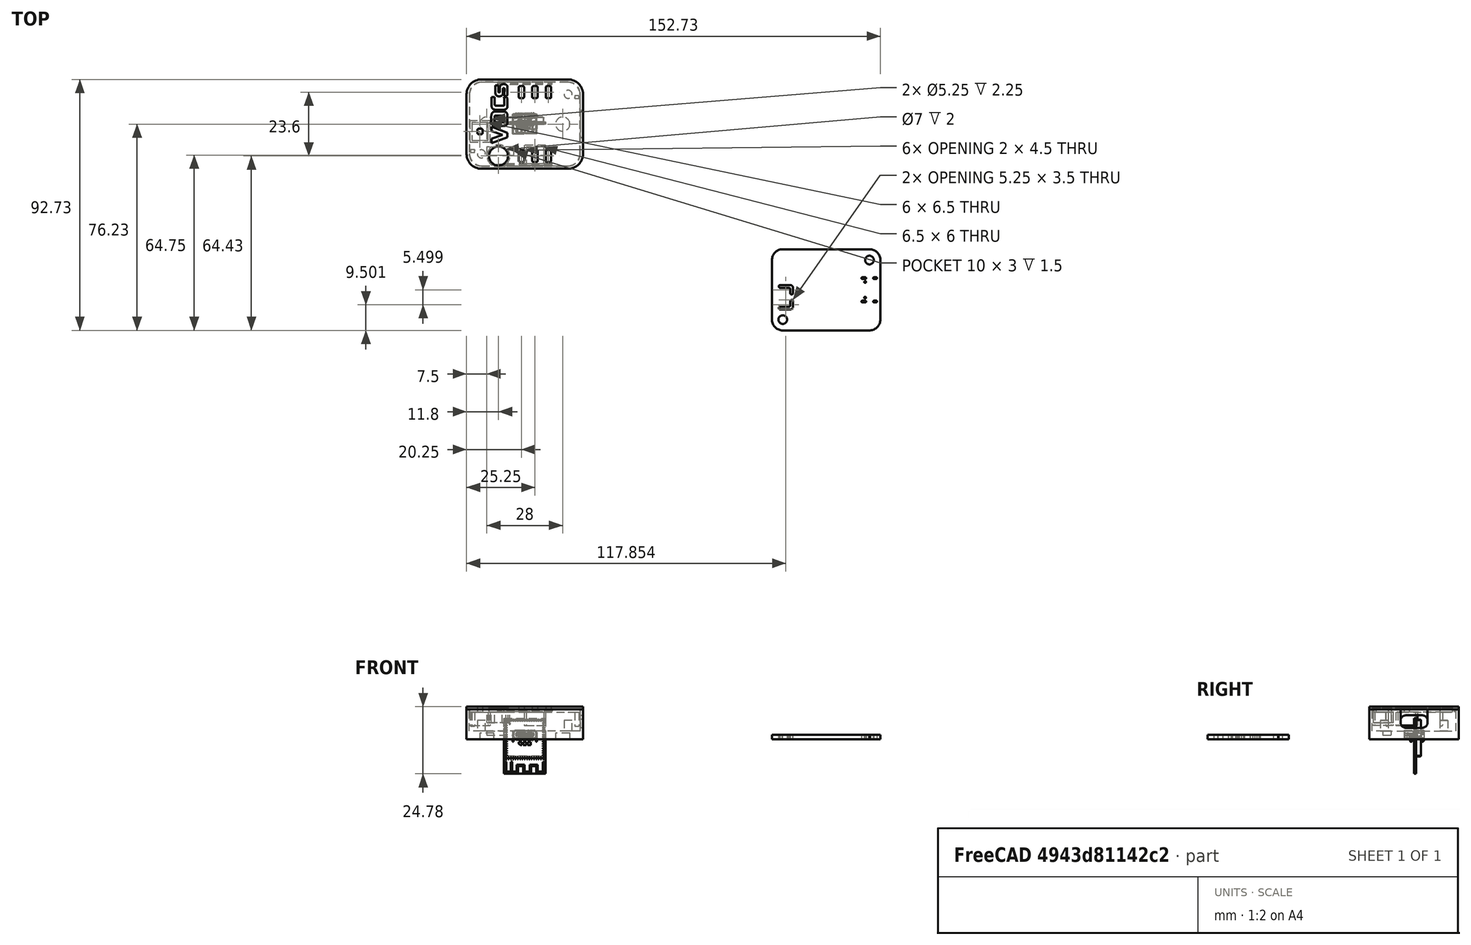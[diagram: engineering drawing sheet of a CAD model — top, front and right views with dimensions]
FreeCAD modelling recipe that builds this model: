
FCSTD DOCUMENT  (FreeCAD 1.0R39109 (Git))
Label: VOCaware_housing
License: All rights reserved
LicenseURL: http://en.wikipedia.org/wiki/All_rights_reserved
objects: Part::Part2DObjectPython×46, Part::Extrusion×36, Part::Feature×28, App::Part×28, Part::Cut×21, Part::Fillet×5, Part::Chamfer×2, Spreadsheet::Sheet×1, App::LinkGroup×1, Part::Fuse×1
note: 139 computed .brp shape members not serialized (recipe doc carries the construction recipe); baked Part::Feature solids carry a one-line shape summary decoded from their .brp

FEATURE [Part::Feature] Part__Feature  label="C_0402_1005Metric"
  shape: bbox 1 x 0.5 x 0.5 mm, 28 faces (baked)
FEATURE [App::Part] C_0402_1005Metric  label="C_0402_1005Metric001"
  Group = -> [Part__Feature]
  Origin = -> Origin
  Placement = pos=(121.23,-72.75,1.65) rot=(0,0,-1;1.5708rad)
FEATURE [Part::Feature] Part__Feature001  label="C_0402_1005Metric002"
  shape: bbox 1 x 0.5 x 0.5 mm, 28 faces (baked)
FEATURE [App::Part] C_0402_1005Metric001  label="C_0402_1005Metric003"
  Group = -> [Part__Feature001]
  Origin = -> Origin001
  Placement = pos=(94.73,-61.98,1.65) rot=(0,0,1;3.14159rad)
FEATURE [Part::Feature] Part__Feature002  label="R_0402_1005Metric"
  shape: bbox 1 x 0.5 x 0.35 mm, 26 faces (baked)
FEATURE [App::Part] R_0402_1005Metric  label="R_0402_1005Metric001"
  Group = -> [Part__Feature002]
  Origin = -> Origin002
  Placement = pos=(126.23,-67.72,1.65) rot=(0,0,1;1.5708rad)
FEATURE [Part::Feature] Part__Feature003  label="R_0402_1005Metric002"
  shape: bbox 1 x 0.5 x 0.35 mm, 26 faces (baked)
FEATURE [App::Part] R_0402_1005Metric001  label="R_0402_1005Metric003"
  Group = -> [Part__Feature003]
  Origin = -> Origin003
  Placement = pos=(119.23,-55.23,1.65) rot=(0,0,1;1.5708rad)
FEATURE [Part::Feature] Part__Feature004  label="C_0402_1005Metric004"
  shape: bbox 1 x 0.5 x 0.5 mm, 28 faces (baked)
FEATURE [App::Part] C_0402_1005Metric002  label="C_0402_1005Metric005"
  Group = -> [Part__Feature004]
  Origin = -> Origin004
  Placement = pos=(121.23,-63.23,1.65) rot=(0,0,1;0rad)
FEATURE [Part::Feature] Part__Feature005  label="R_0402_1005Metric004"
  shape: bbox 1 x 0.5 x 0.35 mm, 26 faces (baked)
FEATURE [App::Part] R_0402_1005Metric002  label="R_0402_1005Metric005"
  Group = -> [Part__Feature005]
  Origin = -> Origin005
  Placement = pos=(100.48,-65.73,1.65) rot=(0,0,1;1.5708rad)
FEATURE [Part::Feature] Part__Feature006  label="R_0402_1005Metric006"
  shape: bbox 1 x 0.5 x 0.35 mm, 26 faces (baked)
FEATURE [App::Part] R_0402_1005Metric003  label="R_0402_1005Metric007"
  Group = -> [Part__Feature006]
  Origin = -> Origin006
  Placement = pos=(114.23,-70.78,1.65) rot=(0,0,1;3.14159rad)
FEATURE [Part::Feature] Part__Feature007  label="C_0402_1005Metric006"
  shape: bbox 1 x 0.5 x 0.5 mm, 28 faces (baked)
FEATURE [App::Part] C_0402_1005Metric003  label="C_0402_1005Metric007"
  Group = -> [Part__Feature007]
  Origin = -> Origin007
  Placement = pos=(117.48,-73.78,1.65) rot=(0,0,-1;1.5708rad)
FEATURE [Part::Feature] Part__Feature008  label="R_0402_1005Metric008"
  shape: bbox 1 x 0.5 x 0.35 mm, 26 faces (baked)
FEATURE [App::Part] R_0402_1005Metric004  label="R_0402_1005Metric009"
  Group = -> [Part__Feature008]
  Origin = -> Origin008
  Placement = pos=(104.48,-70.98,1.65) rot=(0,0,1;1.5708rad)
FEATURE [Part::Feature] Part__Feature009  label="SOT_23"
  shape: bbox 2.5 x 3 x 1.2 mm, 76 faces (baked)
FEATURE [App::Part] SOT_23  label="SOT-23"
  Group = -> [Part__Feature009]
  Origin = -> Origin009
  Placement = pos=(107.293,-72.93,1.65) rot=(0,0,1;3.14159rad)
FEATURE [Part::Feature] Part__Feature010  label="ASSEMBLY"
  shape: bbox 2.54 x 2.44 x 0.95 mm, 50 faces, 8 solids (baked)
FEATURE [App::Part] SGP40_D_R4  label="SGP40-D-R4"
  Group = -> [Part__Feature010]
  Origin = -> Origin010
  Placement = pos=(114.98,-73.03,1.65) rot=(0,0,1;0rad)
FEATURE [Part::Feature] Part__Feature011  label="R_0402_1005Metric010"
  shape: bbox 1 x 0.5 x 0.35 mm, 26 faces (baked)
FEATURE [App::Part] R_0402_1005Metric005  label="R_0402_1005Metric011"
  Group = -> [Part__Feature011]
  Origin = -> Origin011
  Placement = pos=(127.23,-67.72,1.65) rot=(0,0,1;1.5708rad)
FEATURE [Part::Feature] Part__Feature012  label="C_0402_1005Metric008"
  shape: bbox 1 x 0.5 x 0.5 mm, 28 faces (baked)
FEATURE [App::Part] C_0402_1005Metric004  label="C_0402_1005Metric009"
  Group = -> [Part__Feature012]
  Origin = -> Origin012
  Placement = pos=(119.73,-63.5,1.65) rot=(0,0,-1;1.5708rad)
FEATURE [Part::Feature] Part__Feature013  label="C_0603_1608Metric"
  shape: bbox 1.6 x 0.8 x 0.8 mm, 28 faces (baked)
FEATURE [App::Part] C_0603_1608Metric  label="C_0603_1608Metric001"
  Group = -> [Part__Feature013]
  Origin = -> Origin013
  Placement = pos=(100.23,-55.23,1.65) rot=(0,0,1;1.5708rad)
FEATURE [Part::Feature] Part__Feature014  label="R_0402_1005Metric012"
  shape: bbox 1 x 0.5 x 0.35 mm, 26 faces (baked)
FEATURE [App::Part] R_0402_1005Metric006  label="R_0402_1005Metric013"
  Group = -> [Part__Feature014]
  Origin = -> Origin014
  Placement = pos=(100.48,-63.23,1.65) rot=(0,0,-1;1.5708rad)
FEATURE [Part::Feature] Part__Feature015  label="R_0402_1005Metric014"
  shape: bbox 1 x 0.5 x 0.35 mm, 26 faces (baked)
FEATURE [App::Part] R_0402_1005Metric007  label="R_0402_1005Metric015"
  Group = -> [Part__Feature015]
  Origin = -> Origin015
  Placement = pos=(104.48,-73.23,1.65) rot=(0,0,-1;1.5708rad)
FEATURE [Part::Feature] Part__Feature016  label="C_0402_1005Metric010"
  shape: bbox 1 x 0.5 x 0.5 mm, 28 faces (baked)
FEATURE [App::Part] C_0402_1005Metric005  label="C_0402_1005Metric011"
  Group = -> [Part__Feature016]
  Origin = -> Origin016
  Placement = pos=(112.48,-72.78,1.65) rot=(0,0,-1;1.5708rad)
FEATURE [Part::Feature] Part__Feature017  label="USB_C_Receptacle_16P_TopMnt_Horizontal_GCT_USB4105-xx-A"
  shape: bbox 8.94 x 7.78 x 4.26 mm, 646 faces, 36 solids (baked)
FEATURE [App::Part] USB_C_Receptacle_GCT_USB4105_xx_A_16P_TopMnt_Horizontal  label="USB_C_Receptacle_GCT_USB4105-xx-A_16P_TopMnt_Horizontal"
  Group = -> [Part__Feature017]
  Origin = -> Origin017
  Placement = pos=(128.23,-61.23,1.65) rot=(0,0,1;1.5708rad)
FEATURE [Part::Feature] Part__Feature018  label="ASSEMBLY001"
  shape: bbox 4.91 x 3.65 x 1.6 mm, 42 faces, 7 solids (baked)
FEATURE [App::Part] PTS820J25MSMTRLFS
  Group = -> [Part__Feature018]
  Origin = -> Origin018
  Placement = pos=(126.23,-72.23,1.65) rot=(0,0,1;3.14159rad)
FEATURE [Part::Feature] Part__Feature019  label="C_0402_1005Metric012"
  shape: bbox 1 x 0.5 x 0.5 mm, 28 faces (baked)
FEATURE [App::Part] C_0402_1005Metric006  label="C_0402_1005Metric013"
  Group = -> [Part__Feature019]
  Origin = -> Origin019
  Placement = pos=(100.23,-58.23,1.65) rot=(0,0,-1;1.5708rad)
FEATURE [Part::Feature] Part__Feature020  label="R_0402_1005Metric016"
  shape: bbox 1 x 0.5 x 0.35 mm, 26 faces (baked)
FEATURE [App::Part] R_0402_1005Metric008  label="R_0402_1005Metric017"
  Group = -> [Part__Feature020]
  Origin = -> Origin020
  Placement = pos=(109.98,-72.73,1.65) rot=(0,0,1;1.5708rad)
FEATURE [Part::Feature] Part__Feature021  label="C_0402_1005Metric014"
  shape: bbox 1 x 0.5 x 0.5 mm, 28 faces (baked)
FEATURE [App::Part] C_0402_1005Metric007  label="C_0402_1005Metric015"
  Group = -> [Part__Feature021]
  Origin = -> Origin021
  Placement = pos=(119.23,-53.23,1.65) rot=(0,0,1;1.5708rad)
FEATURE [Part::Feature] Part__Feature022  label="C_0402_1005Metric016"
  shape: bbox 1 x 0.5 x 0.5 mm, 28 faces (baked)
FEATURE [App::Part] C_0402_1005Metric008  label="C_0402_1005Metric017"
  Group = -> [Part__Feature022]
  Origin = -> Origin022
  Placement = pos=(121.23,-53.75,1.65) rot=(0,0,1;1.5708rad)
FEATURE [Part::Feature] Part__Feature023  label="ESP32-S3-MINI-1-N8"
  shape: bbox 15.4 x 2.552 x 20.5 mm, 1094 faces, 98 solids (baked)
FEATURE [App::Part] ESP32_S3_MINI_1_N8  label="ESP32-S3-MINI-1-N009"
  Group = -> [Part__Feature023]
  Origin = -> Origin023
  Placement = pos=(109.93,-60.2,1.65) rot=(1,0,0;1.5708rad)
FEATURE [Part::Feature] Part__Feature024  label="C_0402_1005Metric018"
  shape: bbox 1 x 0.5 x 0.5 mm, 28 faces (baked)
FEATURE [App::Part] C_0402_1005Metric009  label="C_0402_1005Metric019"
  Group = -> [Part__Feature024]
  Origin = -> Origin024
  Placement = pos=(101.96,-70.48,1.65) rot=(0,0,1;3.14159rad)
FEATURE [Part::Feature] Part__Feature025  label="Fuse_0603_1608Metric"
  shape: bbox 1.6 x 0.8 x 0.45 mm, 26 faces (baked)
FEATURE [App::Part] Fuse_0603_1608Metric  label="Fuse_0603_1608Metric001"
  Group = -> [Part__Feature025]
  Origin = -> Origin025
  Placement = pos=(121.692,-57.48,1.65) rot=(0,0,1;0rad)
FEATURE [Part::Feature] Part__Feature026  label="ASSEMBLY002"
  shape: bbox 1.84 x 1.5 x 0.69 mm, 30 faces, 5 solids (baked)
FEATURE [App::Part] SHT40_AD1F_R2  label="SHT40-AD1F-R2"
  Group = -> [Part__Feature026]
  Origin = -> Origin026
  Placement = pos=(94.78,-64.03,1.65) rot=(0,0,1;1.5708rad)
FEATURE [Part::Feature] Part__Feature027  label="VOCaware_PCB"
  shape: bbox 40 x 30 x 1.6 mm, 58 faces (baked)
FEATURE [App::Part] VOCaware_1  label="VOCaware 1"
  Group = -> [C_0402_1005Metric,C_0402_1005Metric001,R_0402_1005Metric,R_0402_1005Metric001,C_0402_1005Metric002,R_0402_1005Metric002,R_0402_1005Metric003,C_0402_1005Metric003,R_0402_1005Metric004,SOT_23,SGP40_D_R4,R_0402_1005Metric005,C_0402_1005Metric004,C_0603_1608Metric,R_0402_1005Metric006,R_0402_1005Metric007,C_0402_1005Metric005,USB_C_Receptacle_GCT_USB4105_xx_A_16P_TopMnt_Horizontal,PTS820J25MSMTRLFS,+9 more]
  Origin = -> Origin027
  Placement = pos=(-111.22,61.23,3) rot=(0,0,1;0rad)
  expr: .Placement.Base.x = -111.22 mm
  expr: .Placement.Base.y = 61.23 mm
  expr: .Placement.Base.z = <<params>>.housing_back_thickness
FEATURE [Part::Part2DObjectPython] Rectangle  label="pcb_outline"  # Draft 2D object (typed FeaturePython)
  Area = 1186.27
  ChamferSize = 0
  Columns = 1
  FilletRadius = 4
  Height = 30
  Length = 40
  MakeFace = true
  Placement = pos=(-20,-15,0) rot=(0,0,1;0rad)
  Rows = 1
  expr: .Placement.Base.x = -<<params>>.PCB_width / 2
  expr: .Placement.Base.y = -<<params>>.PCB_length / 2
  expr: FilletRadius = <<params>>.PCB_corner_rad
  expr: Height = <<params>>.PCB_length
  expr: Length = <<params>>.PCB_width
FEATURE [Spreadsheet::Sheet] Spreadsheet  label="params"
  cells = A2='PCB_width; B2(PCB_width)==40 mm; D2='mag_diam; E2(mag_diam)==5 mm; G2='clearance; H2(clearance)==0.5 mm; J2='usb_slit_length; K2(usb_slit_length)==10 mm; M2='usb_bot_clearance; N2(usb_bot_clearance)==0.4 mm; A3='PCB_length; B3(PCB_length)==30 mm; D3='mag_height; E3(mag_height)==2 mm; G3='housing_thickness; H3(housing_thickness)==1 mm; J3='usb_slit_height; K3(usb_slit_height)==3.8 mm; M3='sep_thickness; N3(sep_thickness)==0.7 mm; A4='PCB_corner_rad; B4(PCB_corner_rad)==4 mm; D4='magnet_pos_x; E4(mag_pos_x)==14 mm; G4='housing_back_thickness; H4(housing_back_thickness)==3 mm; J4='M3_clearance; K4(M3_clearance)==0.1 mm; A5='PCB_M3; B5(PCB_M3)==3.2 mm; D5='magnet_clearance; E5(mag_clearance)==0.25 mm; G5='housing_middle_height; H5(housing_middle_height)==8 mm; J5='M3_bottom_height; K5(m3_bottom_height)==4 mm; A6='PCB_height; B6(PCB_height)==1.6 mm; A8='sgp_pos_x; B8(sgp_pos_x)==-PCB_width / 2 + 20.5 mm; D8='sht_pos_x; E8(sht_pos_x)==-PCB_width / 2 + 0.48 mm; G8='led_pos_x; H8(led_pos_x)==-PCB_width / 2 + 10.3 mm - led_width / 2; J8='press_fit_pos_x; K8(press_fit_pos_x)==PCB_width / 2 - press_fit_width; A9='sgp_pos_y; B9(sgp_pos_y)==-PCB_length / 2 + 0.52 mm; D9='sht_pos_y; E9(sht_pos_y)==-PCB_length / 2 + 9.02 mm; G9='led_pos_y; H9(led_pos_y)==-PCB_length / 2 + 3.2 mm - led_height / 2; J9='press_fit_pos_y; K9(press_fit_pos_y)==PCB_length / 2 - PCB_corner_rad - clearance - press_fit_height; A10='sgp_width; B10(sgp_width)==6.5 mm; D10='sht_width; E10(sht_width)==6 mm; G10='led_width; H10(led_width)==6.5 mm; J10='press_fit_width; K10(press_fit_width)==1.5 mm; A11='sgp_length; B11(sgp_length)==6 mm; D11='sht_length; E11(sht_length)==6.5 mm; G11='led_height; H11(led_height)==6.5 mm; J11='press_fit_height; K11(press_fit_height)==1 mm; J12='press_fit_length; K12(press_fit_length)==housing_middle_height - lid_inlet_depth - PCB_height - mag_clearance; A13='snap_fit_width; B13(snap_fit_width)==20 mm; D13='lid_clearance; E13(lid_clearance)==0.2 mm; G13='led_circle_dia; H13(led_circle_dia)==7 mm; A14='snap_fit_height; B14(snap_fit_height)==0.6 mm; D14='lid_top_height; E14(lid_top_height)==1 mm; G14='led_cover_thickness; H14(led_cover_thickness)==0.4 mm; A15='snap_fit_depth; B15(snap_fit_depth)==0.6 mm; D15='lid_inlet_depth; E15(lid_inlet_depth)==1 mm; A16='snap_fit_clearance; B16(snap_fit_clearance)==0.1 mm; D16='lid_breakout_offset; E16(lid_breakout_offset)==0 mm; F16=13; A18='gnd_bug_x; B18(gnd_bug_x)==-14 mm; D18='sgp_cutout_width; E18(sgp_cutout_width)==2 mm; G18='sht_cutout_width; H18(sht_cutout_width)==2 mm; A19='gnd_bug_y; B19(gnd_bug_y)==-11.5 mm; D19='sgp_cutout_height; E19(sgp_cutout_height)==4.5 mm; G19='sht_cutout_height; H19(sht_cutout_height)==2 mm; A20='gnd_bug_width; B20(gnd_bug_width)==10 mm; D20='cutout_distance; E20(cutout_distance)==5 mm; G20='led_sep_depth; H20(led_sep_depth)==4 mm; A21='gnd_bug_height; B21(gnd_bug_height)==3 mm; A22='gnd_bug_depth; B22(gnd_bug_depth)==1.5 mm
FEATURE [Part::Part2DObjectPython] Arc  label="pcb_outl_corner_tl"  # Draft 2D object (typed FeaturePython)
  Area = 0
  FirstAngle = 90
  LastAngle = 180
  MakeFace = true
  Placement = pos=(-16,11,0) rot=(0,0,1;0rad)
  Radius = 4
  expr: .Placement.Base.x = -<<params>>.PCB_width / 2 + <<params>>.PCB_corner_rad
  expr: .Placement.Base.y = <<params>>.PCB_length / 2 - <<params>>.PCB_corner_rad
  expr: Radius = <<params>>.PCB_corner_rad
FEATURE [Part::Part2DObjectPython] Arc001  label="pcb_outl_corner_tr"  # Draft 2D object (typed FeaturePython)
  Area = 0
  FirstAngle = 0
  LastAngle = 90
  MakeFace = true
  Placement = pos=(16,11,0) rot=(0,0,1;0rad)
  Radius = 4
  expr: .Placement.Base.x = <<params>>.PCB_width / 2 - <<params>>.PCB_corner_rad
  expr: .Placement.Base.y = <<params>>.PCB_length / 2 - <<params>>.PCB_corner_rad
  expr: Radius = <<params>>.PCB_corner_rad
FEATURE [Part::Part2DObjectPython] Arc002  label="pcb_outl_corner_bl"  # Draft 2D object (typed FeaturePython)
  Area = 0
  FirstAngle = 180
  LastAngle = 270
  MakeFace = true
  Placement = pos=(-16,-11,0) rot=(0,0,1;0rad)
  Radius = 4
  expr: .Placement.Base.x = -<<params>>.PCB_width / 2 + <<params>>.PCB_corner_rad
  expr: .Placement.Base.y = -<<params>>.PCB_length / 2 + <<params>>.PCB_corner_rad
  expr: Radius = <<params>>.PCB_corner_rad
FEATURE [Part::Part2DObjectPython] Arc003  label="pcb_outl_corner_br"  # Draft 2D object (typed FeaturePython)
  Area = 0
  FirstAngle = 270
  LastAngle = 0
  MakeFace = true
  Placement = pos=(16,-11,0) rot=(0,0,1;0rad)
  Radius = 4
  expr: .Placement.Base.x = <<params>>.PCB_width / 2 - <<params>>.PCB_corner_rad
  expr: .Placement.Base.y = -<<params>>.PCB_length / 2 + <<params>>.PCB_corner_rad
  expr: Radius = <<params>>.PCB_corner_rad
FEATURE [Part::Part2DObjectPython] Line  label="pcb_outl_line_l"  # Draft 2D object (typed FeaturePython)
  Area = 0
  ChamferSize = 0
  Closed = false
  End = (-20,11,0)
  FilletRadius = 0
  Length = 22
  MakeFace = true
  Placement = pos=(-20,-11,0) rot=(0,0,1;0rad)
  Points = (2) [(0,0,0),(0,22,0)]
  Start = (-20,-11,0)
  Subdivisions = 0
  expr: .End.x = -<<params>>.PCB_width / 2
  expr: .End.y = <<params>>.PCB_length / 2 - <<params>>.PCB_corner_rad
  expr: .Placement.Base.x = -<<params>>.PCB_width / 2
  expr: .Placement.Base.y = -<<params>>.PCB_length / 2 + <<params>>.PCB_corner_rad
  expr: .Start.x = -<<params>>.PCB_width / 2
  expr: .Start.y = -<<params>>.PCB_length / 2 + <<params>>.PCB_corner_rad
  expr: Length = <<params>>.PCB_length - 2 * <<params>>.PCB_corner_rad
FEATURE [Part::Part2DObjectPython] Line001  label="pcb_outl_line_r"  # Draft 2D object (typed FeaturePython)
  Area = 0
  ChamferSize = 0
  Closed = false
  End = (20,11,0)
  FilletRadius = 0
  Length = 22
  MakeFace = true
  Placement = pos=(-20,-11,0) rot=(0,0,1;0rad)
  Points = (2) [(40,0,0),(40,22,0)]
  Start = (20,-11,0)
  Subdivisions = 0
  expr: .End.x = <<params>>.PCB_width / 2
  expr: .End.y = <<params>>.PCB_length / 2 - <<params>>.PCB_corner_rad
  expr: .Placement.Base.x = -<<params>>.PCB_width / 2
  expr: .Placement.Base.y = -<<params>>.PCB_length / 2 + <<params>>.PCB_corner_rad
  expr: .Start.x = +<<params>>.PCB_width / 2
  expr: .Start.y = -<<params>>.PCB_length / 2 + <<params>>.PCB_corner_rad
  expr: Length = <<params>>.PCB_length - 2 * <<params>>.PCB_corner_rad
FEATURE [Part::Part2DObjectPython] Line002  label="pcb_outl_line_t"  # Draft 2D object (typed FeaturePython)
  Area = 0
  ChamferSize = 0
  Closed = false
  End = (-16,15,0)
  FilletRadius = 0
  Length = 32
  MakeFace = true
  Placement = pos=(-20,-11,0) rot=(0,0,1;0rad)
  Points = (2) [(36,26,0),(4,26,0)]
  Start = (16,15,0)
  Subdivisions = 0
  expr: .End.x = -<<params>>.PCB_width / 2 + <<params>>.PCB_corner_rad
  expr: .End.y = <<params>>.PCB_length / 2
  expr: .Placement.Base.x = -<<params>>.PCB_width / 2
  expr: .Placement.Base.y = -<<params>>.PCB_length / 2 + <<params>>.PCB_corner_rad
  expr: .Start.x = <<params>>.PCB_width / 2 - <<params>>.PCB_corner_rad
  expr: .Start.y = <<params>>.PCB_length / 2
  expr: Length = <<params>>.PCB_width - 2 * <<params>>.PCB_corner_rad
FEATURE [Part::Part2DObjectPython] Line003  label="pcb_outl_line_b"  # Draft 2D object (typed FeaturePython)
  Area = 0
  ChamferSize = 0
  Closed = false
  End = (-16,-15,0)
  FilletRadius = 0
  Length = 32
  MakeFace = true
  Placement = pos=(-20,-11,0) rot=(0,0,1;0rad)
  Points = (2) [(36,-4,0),(4,-4,0)]
  Start = (16,-15,0)
  Subdivisions = 0
  expr: .End.x = -<<params>>.PCB_width / 2 + <<params>>.PCB_corner_rad
  expr: .End.y = -<<params>>.PCB_length / 2
  expr: .Placement.Base.x = -<<params>>.PCB_width / 2
  expr: .Placement.Base.y = -<<params>>.PCB_length / 2 + <<params>>.PCB_corner_rad
  expr: .Start.x = <<params>>.PCB_width / 2 - <<params>>.PCB_corner_rad
  expr: .Start.y = -<<params>>.PCB_length / 2
  expr: Length = <<params>>.PCB_width - 2 * <<params>>.PCB_corner_rad
FEATURE [Part::Part2DObjectPython] Circle  label="m3_bl"  # Draft 2D object (typed FeaturePython)
  Area = 7.06858
  FirstAngle = 0
  LastAngle = 0
  MakeFace = true
  Placement = pos=(-16,-11,3) rot=(0,0,1;0rad)
  Radius = 1.5
  expr: .Placement.Base.x = -<<params>>.PCB_width / 2 + <<params>>.PCB_corner_rad
  expr: .Placement.Base.y = -<<params>>.PCB_length / 2 + <<params>>.PCB_corner_rad
  expr: .Placement.Base.z = <<params>>.housing_back_thickness
  expr: Radius = <<params>>.PCB_M3 / 2 - <<params>>.M3_clearance
FEATURE [Part::Part2DObjectPython] Circle001  label="m3_tr"  # Draft 2D object (typed FeaturePython)
  Area = 7.06858
  FirstAngle = 0
  LastAngle = 0
  MakeFace = true
  Placement = pos=(16,11,3) rot=(0,0,1;0rad)
  Radius = 1.5
  expr: .Placement.Base.x = +<<params>>.PCB_width / 2 - <<params>>.PCB_corner_rad
  expr: .Placement.Base.y = <<params>>.PCB_length / 2 - <<params>>.PCB_corner_rad
  expr: .Placement.Base.z = <<params>>.housing_back_thickness
  expr: Radius = <<params>>.PCB_M3 / 2 - <<params>>.M3_clearance
FEATURE [Part::Part2DObjectPython] Rectangle001  label="inner_housing"  # Draft 2D object (typed FeaturePython)
  Area = 1253.62
  ChamferSize = 0
  Columns = 1
  FilletRadius = 4.5
  Height = 31
  Length = 41
  MakeFace = true
  Placement = pos=(-20.5,-15.5,3) rot=(0,0,1;0rad)
  Rows = 1
  expr: .Placement.Base.x = -<<params>>.PCB_width / 2 - <<params>>.clearance
  expr: .Placement.Base.y = -<<params>>.PCB_length / 2 - <<params>>.clearance
  expr: .Placement.Base.z = <<params>>.housing_back_thickness
  expr: FilletRadius = <<params>>.PCB_corner_rad + <<params>>.clearance
  expr: Height = <<params>>.PCB_length + 2 * <<params>>.clearance
  expr: Length = <<params>>.PCB_width + 2 * <<params>>.clearance
FEATURE [Part::Part2DObjectPython] Rectangle002  label="outer_housing"  # Draft 2D object (typed FeaturePython)
  Area = 1393.03
  ChamferSize = 0
  Columns = 1
  FilletRadius = 5.5
  Height = 33
  Length = 43
  MakeFace = true
  Placement = pos=(-21.5,-16.5,0) rot=(0,0,1;0rad)
  Rows = 1
  expr: .Placement.Base.x = -<<params>>.PCB_width / 2 - <<params>>.clearance - <<params>>.housing_thickness
  expr: .Placement.Base.y = -<<params>>.PCB_length / 2 - <<params>>.clearance - <<params>>.housing_thickness
  expr: FilletRadius = <<params>>.PCB_corner_rad + <<params>>.clearance + <<params>>.housing_thickness
  expr: Height = <<params>>.PCB_length + 2 * <<params>>.clearance + 2 * <<params>>.housing_thickness
  expr: Length = <<params>>.PCB_width + 2 * <<params>>.clearance + 2 * <<params>>.housing_thickness
FEATURE [App::LinkGroup] LinkGroup  label="pcb_outline_detailed"
  ElementList = -> [Arc,Arc001,Arc002,Arc003,Line,Line001,Line002,Line003]
  LinkMode = 0
FEATURE [Part::Part2DObjectPython] Rectangle003  label="usb_slit"  # Draft 2D object (typed FeaturePython)
  Area = 10
  ChamferSize = 0
  Columns = 1
  FilletRadius = 0
  Height = 10
  Length = 1
  MakeFace = true
  Placement = pos=(20.5,-5,4.2) rot=(0,0,1;0rad)
  Rows = 1
  expr: .Placement.Base.x = <<params>>.PCB_width / 2 + <<params>>.clearance
  expr: .Placement.Base.y = -<<params>>.usb_slit_length / 2
  expr: .Placement.Base.z = <<params>>.housing_back_thickness + <<params>>.PCB_height - <<params>>.usb_bot_clearance
  expr: Height = <<params>>.usb_slit_length
  expr: Length = <<params>>.housing_thickness
FEATURE [Part::Part2DObjectPython] Circle002  label="mag_l"  # Draft 2D object (typed FeaturePython)
  Area = 21.6475
  FirstAngle = 0
  LastAngle = 0
  MakeFace = true
  Placement = pos=(14,0,0) rot=(0,0,1;0rad)
  Radius = 2.625
  expr: .Placement.Base.x = <<params>>.mag_pos_x
  expr: Radius = <<params>>.mag_diam / 2 + <<params>>.mag_clearance / 2
FEATURE [Part::Part2DObjectPython] Circle003  label="mag_r"  # Draft 2D object (typed FeaturePython)
  Area = 21.6475
  FirstAngle = 0
  LastAngle = 0
  MakeFace = true
  Placement = pos=(-14,0,0) rot=(0,0,1;0rad)
  Radius = 2.625
  expr: .Placement.Base.x = -<<params>>.mag_pos_x
  expr: Radius = <<params>>.mag_diam / 2 + <<params>>.mag_clearance / 2
FEATURE [Part::Part2DObjectPython] Rectangle004  label="sgp_outline"  # Draft 2D object (typed FeaturePython)
  Area = 39
  ChamferSize = 0
  Columns = 1
  FilletRadius = 0
  Height = 6
  Length = 6.5
  MakeFace = true
  Placement = pos=(0.5,-14.48,10) rot=(0,0,1;0rad)
  Rows = 1
  expr: .Placement.Base.x = <<params>>.sgp_pos_x
  expr: .Placement.Base.y = <<params>>.sgp_pos_y
  expr: .Placement.Base.z = <<params>>.housing_back_thickness + <<params>>.housing_middle_height + <<params>>.lid_breakout_offset - <<params>>.lid_inlet_depth
  expr: Height = <<params>>.sgp_length
  expr: Length = <<params>>.sgp_width
FEATURE [Part::Part2DObjectPython] Rectangle005  label="sht_outline"  # Draft 2D object (typed FeaturePython)
  Area = 39
  ChamferSize = 0
  Columns = 1
  FilletRadius = 0
  Height = 6.5
  Length = 6
  MakeFace = true
  Placement = pos=(-19.52,-5.98,10) rot=(0,0,1;0rad)
  Rows = 1
  expr: .Placement.Base.x = <<params>>.sht_pos_x
  expr: .Placement.Base.y = <<params>>.sht_pos_y
  expr: .Placement.Base.z = <<params>>.housing_back_thickness + <<params>>.housing_middle_height + <<params>>.lid_breakout_offset - <<params>>.lid_inlet_depth
  expr: Height = <<params>>.sht_length
  expr: Length = <<params>>.sht_width
FEATURE [Part::Part2DObjectPython] Rectangle006  label="led_outline"  # Draft 2D object (typed FeaturePython)
  Area = 42.25
  ChamferSize = 0
  Columns = 1
  FilletRadius = 0
  Height = 6.5
  Length = 6.5
  MakeFace = true
  Placement = pos=(-12.95,-15.05,0) rot=(0,0,1;0rad)
  Rows = 1
  expr: .Placement.Base.x = <<params>>.led_pos_x
  expr: .Placement.Base.y = <<params>>.led_pos_y
  expr: Height = <<params>>.led_height
  expr: Length = <<params>>.led_width
FEATURE [Part::Extrusion] Extrude  label="out_extrude"
  Base = -> Rectangle002
  Dir = (0,0,1)
  DirMode = 2
  FaceMakerClass = Part::FaceMakerBullseye
  FaceMakerMode = 3
  LengthFwd = 11
  LengthRev = 0
  Solid = false
  Symmetric = false
  expr: LengthFwd = <<params>>.housing_back_thickness + <<params>>.housing_middle_height
FEATURE [Part::Extrusion] Extrude001  label="in_extrude"
  Base = -> Rectangle001
  Dir = (0,0,1)
  DirMode = 2
  FaceMakerClass = Part::FaceMakerBullseye
  FaceMakerMode = 3
  LengthFwd = 8
  LengthRev = 0
  Solid = false
  Symmetric = false
  expr: LengthFwd = <<params>>.housing_middle_height
FEATURE [Part::Cut] Cut  label="housing_base"
  Base = -> Extrude
  Refine = true
  Tool = -> Extrude001
FEATURE [Part::Extrusion] Extrude002  label="m3_pole_bl"
  Base = -> Circle
  Dir = (0,0,1)
  DirMode = 2
  FaceMakerClass = Part::FaceMakerBullseye
  FaceMakerMode = 3
  LengthFwd = 4
  LengthRev = 0
  Solid = false
  Symmetric = false
  expr: LengthFwd = <<params>>.m3_bottom_height
FEATURE [Part::Extrusion] Extrude003  label="m3_pole_tr"
  Base = -> Circle001
  Dir = (0,0,1)
  DirMode = 2
  FaceMakerClass = Part::FaceMakerBullseye
  FaceMakerMode = 3
  LengthFwd = 4
  LengthRev = 0
  Solid = false
  Symmetric = false
  expr: LengthFwd = <<params>>.m3_bottom_height
FEATURE [Part::Extrusion] Extrude004
  Base = -> Rectangle003
  Dir = (0,0,1)
  DirMode = 2
  FaceMakerClass = Part::FaceMakerBullseye
  FaceMakerMode = 3
  LengthFwd = 6.8
  LengthRev = 0
  Solid = false
  Symmetric = false
  expr: LengthFwd = <<params>>.housing_middle_height - <<params>>.PCB_height + <<params>>.usb_bot_clearance
FEATURE [Part::Fillet] Fillet
  Base = -> Extrude004
  EdgeLinks = -> Extrude004 [Edge3,Edge9]
  Edges = 2 edges r=2: [Edge3,Edge9]
FEATURE [Part::Cut] Cut001  label="usb_slit_cut"
  Base = -> Cut
  Refine = true
  Tool = -> Fillet
FEATURE [Part::Part2DObjectPython] Rectangle007  label="snap_base_top"  # Draft 2D object (typed FeaturePython)
  Area = 12
  ChamferSize = 0
  Columns = 1
  FilletRadius = 0
  Height = 0.6
  Length = 20
  MakeFace = true
  Placement = pos=(-10,14.9,11) rot=(0,0,1;0rad)
  Rows = 1
  expr: .Placement.Base.x = -<<params>>.snap_fit_width / 2
  expr: .Placement.Base.y = <<params>>.PCB_length / 2 + <<params>>.clearance - <<params>>.snap_fit_depth
  expr: .Placement.Base.z = <<params>>.housing_back_thickness + <<params>>.housing_middle_height
  expr: Height = <<params>>.snap_fit_depth
  expr: Length = <<params>>.snap_fit_width
FEATURE [Part::Part2DObjectPython] Rectangle008  label="snap_base_bot"  # Draft 2D object (typed FeaturePython)
  Area = 12
  ChamferSize = 0
  Columns = 1
  FilletRadius = 0
  Height = 0.6
  Length = 20
  MakeFace = true
  Placement = pos=(-10,-15.5,11) rot=(0,0,1;0rad)
  Rows = 1
  expr: .Placement.Base.x = -<<params>>.snap_fit_width / 2
  expr: .Placement.Base.y = -<<params>>.PCB_length / 2 - <<params>>.clearance
  expr: .Placement.Base.z = <<params>>.housing_back_thickness + <<params>>.housing_middle_height
  expr: Height = <<params>>.snap_fit_depth
  expr: Length = <<params>>.snap_fit_width
FEATURE [Part::Extrusion] Extrude005  label="snap_top_extr"
  Base = -> Rectangle007
  Dir = (0,0,1)
  DirMode = 2
  FaceMakerClass = Part::FaceMakerBullseye
  FaceMakerMode = 3
  LengthFwd = -0.6
  LengthRev = 0
  Solid = false
  Symmetric = false
  expr: LengthFwd = -<<params>>.snap_fit_height
FEATURE [Part::Extrusion] Extrude006  label="snap_bot_extr"
  Base = -> Rectangle008
  Dir = (0,0,1)
  DirMode = 2
  FaceMakerClass = Part::FaceMakerBullseye
  FaceMakerMode = 3
  LengthFwd = -0.6
  LengthRev = 0
  Solid = false
  Symmetric = false
  expr: LengthFwd = -<<params>>.snap_fit_height
FEATURE [Part::Chamfer] Chamfer  label="snap_top_Chamfer"
  Base = -> Extrude005
  EdgeLinks = -> Extrude005 [Edge3]
  Edges = 1 edges r=0.5: [Edge3]
FEATURE [Part::Chamfer] Chamfer001  label="snap_bot_Chamfer"
  Base = -> Extrude006
  EdgeLinks = -> Extrude006 [Edge9]
  Edges = 1 edges r=0.5: [Edge9]
FEATURE [Part::Part2DObjectPython] Rectangle009  label="outer_lid"  # Draft 2D object (typed FeaturePython)
  Area = 1393.03
  ChamferSize = 0
  Columns = 1
  FilletRadius = 5.5
  Height = 33
  Length = 43
  MakeFace = true
  Placement = pos=(-21.5,-16.5,11) rot=(0,0,1;0rad)
  Rows = 1
  expr: .Placement.Base.x = -<<params>>.PCB_width / 2 - <<params>>.clearance - <<params>>.housing_thickness
  expr: .Placement.Base.y = -<<params>>.PCB_length / 2 - <<params>>.clearance - <<params>>.housing_thickness
  expr: .Placement.Base.z = <<params>>.housing_back_thickness + <<params>>.housing_middle_height + <<params>>.lid_breakout_offset
  expr: FilletRadius = <<params>>.PCB_corner_rad + <<params>>.clearance + <<params>>.housing_thickness
  expr: Height = <<params>>.PCB_length + 2 * <<params>>.clearance + 2 * <<params>>.housing_thickness
  expr: Length = <<params>>.PCB_width + 2 * <<params>>.clearance + 2 * <<params>>.housing_thickness
FEATURE [Part::Part2DObjectPython] Rectangle010  label="inner_lid"  # Draft 2D object (typed FeaturePython)
  Area = 1239.26
  ChamferSize = 0
  Columns = 1
  FilletRadius = 4.5
  Height = 30.8
  Length = 40.8
  MakeFace = true
  Placement = pos=(-20.4,-15.4,11) rot=(0,0,1;0rad)
  Rows = 1
  expr: .Placement.Base.x = -<<params>>.PCB_width / 2 - <<params>>.clearance + <<params>>.lid_clearance / 2
  expr: .Placement.Base.y = -<<params>>.PCB_length / 2 - <<params>>.clearance + <<params>>.lid_clearance / 2
  expr: .Placement.Base.z = <<params>>.housing_back_thickness + <<params>>.housing_middle_height + <<params>>.lid_breakout_offset
  expr: FilletRadius = <<params>>.PCB_corner_rad + <<params>>.clearance
  expr: Height = <<params>>.PCB_length + 2 * <<params>>.clearance - <<params>>.lid_clearance
  expr: Length = <<params>>.PCB_width + 2 * <<params>>.clearance - <<params>>.lid_clearance
FEATURE [Part::Extrusion] Extrude007  label="lid_top"
  Base = -> Rectangle009
  Dir = (0,0,1)
  DirMode = 2
  FaceMakerClass = Part::FaceMakerBullseye
  FaceMakerMode = 3
  LengthFwd = 1
  LengthRev = 0
  Solid = false
  Symmetric = false
  expr: LengthFwd = <<params>>.lid_top_height
FEATURE [Part::Extrusion] Extrude008  label="lid_bot"
  Base = -> Rectangle010
  Dir = (0,0,1)
  DirMode = 2
  FaceMakerClass = Part::FaceMakerBullseye
  FaceMakerMode = 3
  LengthFwd = -1
  LengthRev = 0
  Solid = false
  Symmetric = false
  expr: LengthFwd = -<<params>>.lid_inlet_depth
FEATURE [Part::Part2DObjectPython] Rectangle011  label="snap_lid_top"  # Draft 2D object (typed FeaturePython)
  Area = 14.14
  ChamferSize = 0
  Columns = 1
  FilletRadius = 0
  Height = 0.7
  Length = 20.2
  MakeFace = true
  Placement = pos=(-10.1,14.7,11) rot=(0,0,1;0rad)
  Rows = 1
  expr: .Placement.Base.x = -<<params>>.snap_fit_width / 2 - <<params>>.snap_fit_clearance
  expr: .Placement.Base.y = <<params>>.PCB_length / 2 + <<params>>.clearance - <<params>>.snap_fit_depth - <<params>>.snap_fit_clearance - <<params>>.lid_clearance / 2
  expr: .Placement.Base.z = <<params>>.housing_back_thickness + <<params>>.housing_middle_height + <<params>>.lid_breakout_offset
  expr: Height = <<params>>.snap_fit_depth + <<params>>.snap_fit_clearance
  expr: Length = <<params>>.snap_fit_width + 2 * <<params>>.snap_fit_clearance
FEATURE [Part::Part2DObjectPython] Rectangle012  label="snap_lid_bot"  # Draft 2D object (typed FeaturePython)
  Area = 14.14
  ChamferSize = 0
  Columns = 1
  FilletRadius = 0
  Height = 0.7
  Length = 20.2
  MakeFace = true
  Placement = pos=(-10.1,-15.4,11) rot=(0,0,1;0rad)
  Rows = 1
  expr: .Placement.Base.x = -<<params>>.snap_fit_width / 2 - <<params>>.snap_fit_clearance
  expr: .Placement.Base.y = -<<params>>.PCB_length / 2 - <<params>>.clearance + <<params>>.lid_clearance / 2
  expr: .Placement.Base.z = <<params>>.housing_back_thickness + <<params>>.housing_middle_height + <<params>>.lid_breakout_offset
  expr: Height = <<params>>.snap_fit_depth + <<params>>.snap_fit_clearance
  expr: Length = <<params>>.snap_fit_width + 2 * <<params>>.snap_fit_clearance
FEATURE [Part::Extrusion] Extrude009
  Base = -> Rectangle011
  Dir = (0,0,1)
  DirMode = 2
  FaceMakerClass = Part::FaceMakerBullseye
  FaceMakerMode = 3
  LengthFwd = -0.7
  LengthRev = 0
  Solid = false
  Symmetric = false
  expr: LengthFwd = -<<params>>.snap_fit_height - <<params>>.snap_fit_clearance
FEATURE [Part::Extrusion] Extrude010
  Base = -> Rectangle012
  Dir = (0,0,1)
  DirMode = 2
  FaceMakerClass = Part::FaceMakerBullseye
  FaceMakerMode = 3
  LengthFwd = -0.7
  LengthRev = 0
  Solid = false
  Symmetric = false
  expr: LengthFwd = -<<params>>.snap_fit_height - <<params>>.snap_fit_clearance
FEATURE [Part::Cut] Cut002
  Base = -> Extrude008
  Refine = true
  Tool = -> Extrude009
FEATURE [Part::Cut] Cut003  label="lid_snap_cut"
  Base = -> Cut002
  Refine = true
  Tool = -> Extrude010
FEATURE [Part::Extrusion] Extrude011  label="mag_l_extr"
  Base = -> Circle002
  Dir = (0,0,1)
  DirMode = 2
  FaceMakerClass = Part::FaceMakerBullseye
  FaceMakerMode = 3
  LengthFwd = 2.25
  LengthRev = 0
  Solid = false
  Symmetric = false
  expr: LengthFwd = <<params>>.mag_height + <<params>>.mag_clearance
FEATURE [Part::Extrusion] Extrude012  label="mag_r_extr"
  Base = -> Circle003
  Dir = (0,0,1)
  DirMode = 2
  FaceMakerClass = Part::FaceMakerBullseye
  FaceMakerMode = 3
  LengthFwd = 2.25
  LengthRev = 0
  Solid = false
  Symmetric = false
  expr: LengthFwd = <<params>>.mag_height + <<params>>.mag_clearance
FEATURE [Part::Cut] Cut004
  Base = -> Cut001
  Refine = true
  Tool = -> Extrude011
FEATURE [Part::Cut] Cut005  label="bot_w_mag_holes"
  Base = -> Cut004
  Refine = true
  Tool = -> Extrude012
FEATURE [Part::Part2DObjectPython] Rectangle013  label="usb_slit001"  # Draft 2D object (typed FeaturePython)
  Area = 10
  ChamferSize = 0
  Columns = 1
  FilletRadius = 0
  Height = 10
  Length = 1
  MakeFace = true
  Placement = pos=(20.5,-5,4.2) rot=(0,0,1;0rad)
  Rows = 1
  expr: .Placement.Base.x = <<params>>.PCB_width / 2 + <<params>>.clearance
  expr: .Placement.Base.y = -<<params>>.usb_slit_length / 2
  expr: .Placement.Base.z = <<params>>.housing_back_thickness + <<params>>.PCB_height - <<params>>.usb_bot_clearance
  expr: Height = <<params>>.usb_slit_length
  expr: Length = <<params>>.housing_thickness
FEATURE [Part::Extrusion] Extrude013
  Base = -> Rectangle013
  Dir = (0,0,1)
  DirMode = 2
  FaceMakerClass = Part::FaceMakerBullseye
  FaceMakerMode = 3
  LengthFwd = 4.6
  LengthRev = 0
  Solid = false
  Symmetric = false
  expr: LengthFwd = <<params>>.usb_slit_height + 2 * <<params>>.usb_bot_clearance
FEATURE [Part::Fillet] Fillet001
  Base = -> Extrude013
  EdgeLinks = -> Extrude013 [Edge3,Edge9]
  Edges = 2 edges r=2: [Edge3,Edge9]
FEATURE [Part::Fillet] Fillet002
  Base = -> Fillet001
  EdgeLinks = -> Fillet001 [Edge3,Edge13]
  Edges = 2 edges r=2: [Edge3,Edge13]
FEATURE [Part::Part2DObjectPython] Rectangle014  label="usb_slit002"  # Draft 2D object (typed FeaturePython)
  Area = 9.8
  ChamferSize = 0
  Columns = 1
  FilletRadius = 0
  Height = 9.8
  Length = 1
  MakeFace = true
  Placement = pos=(20.5,-4.9,6.2) rot=(0,0,1;0rad)
  Rows = 1
  expr: .Placement.Base.x = <<params>>.PCB_width / 2 + <<params>>.clearance
  expr: .Placement.Base.y = -<<params>>.usb_slit_length / 2 + <<params>>.lid_clearance / 2
  expr: .Placement.Base.z = <<params>>.housing_back_thickness + <<params>>.PCB_height - <<params>>.usb_bot_clearance + 2 mm
  expr: Height = <<params>>.usb_slit_length - <<params>>.lid_clearance
  expr: Length = <<params>>.housing_thickness
FEATURE [Part::Extrusion] Extrude014
  Base = -> Rectangle014
  Dir = (0,0,1)
  DirMode = 2
  FaceMakerClass = Part::FaceMakerBullseye
  FaceMakerMode = 3
  LengthFwd = 4.8
  LengthRev = 0
  Solid = false
  Symmetric = false
  expr: LengthFwd = <<params>>.housing_middle_height - <<params>>.PCB_height + <<params>>.usb_bot_clearance - 2 mm
FEATURE [Part::Cut] Cut006  label="usb_top_cut"
  Base = -> Extrude014
  Refine = true
  Tool = -> Fillet002
  expr: .Placement.Base.z = <<params>>.lid_breakout_offset
FEATURE [Part::Part2DObjectPython] Circle004  label="led_circle_lid"  # Draft 2D object (typed FeaturePython)
  Area = 38.4845
  FirstAngle = 0
  LastAngle = 0
  MakeFace = true
  Placement = pos=(-9.7,-11.8,12) rot=(0,0,1;0rad)
  Radius = 3.5
  expr: .Placement.Base.x = <<params>>.led_pos_x + <<params>>.led_width / 2
  expr: .Placement.Base.y = <<params>>.led_pos_y + <<params>>.led_height / 2
  expr: .Placement.Base.z = <<params>>.housing_back_thickness + <<params>>.housing_middle_height + <<params>>.lid_breakout_offset + <<params>>.lid_top_height
  expr: Radius = <<params>>.led_circle_dia / 2
FEATURE [Part::Extrusion] Extrude015  label="led_lid_cutout"
  Base = -> Circle004
  Dir = (0,0,1)
  DirMode = 2
  FaceMakerClass = Part::FaceMakerBullseye
  FaceMakerMode = 3
  LengthFwd = -2
  LengthRev = 0
  Solid = false
  Symmetric = false
  expr: LengthFwd = -<<params>>.lid_top_height - <<params>>.lid_inlet_depth
FEATURE [Part::Fuse] Fusion  label="lid"
  Base = -> Extrude007
  Refine = true
  Tool = -> Cut003
FEATURE [Part::Cut] Cut007  label="lid_w_led_hole"
  Base = -> Fusion
  Refine = true
  Tool = -> Extrude015
FEATURE [Part::Part2DObjectPython] Circle005  label="led_circle_lid_tranparent"  # Draft 2D object (typed FeaturePython)
  Area = 38.4845
  FirstAngle = 0
  LastAngle = 0
  MakeFace = true
  Placement = pos=(-9.7,-11.8,12) rot=(0,0,1;0rad)
  Radius = 3.5
  expr: .Placement.Base.x = <<params>>.led_pos_x + <<params>>.led_width / 2
  expr: .Placement.Base.y = <<params>>.led_pos_y + <<params>>.led_height / 2
  expr: .Placement.Base.z = <<params>>.housing_back_thickness + <<params>>.housing_middle_height + <<params>>.lid_breakout_offset + <<params>>.lid_top_height
  expr: Radius = <<params>>.led_circle_dia / 2
FEATURE [Part::Extrusion] Extrude016  label="led_cirlcle_trans_extr"
  Base = -> Circle005
  Dir = (0,0,1)
  DirMode = 2
  FaceMakerClass = Part::FaceMakerBullseye
  FaceMakerMode = 3
  LengthFwd = -0.4
  LengthRev = 0
  Solid = false
  Symmetric = false
  expr: LengthFwd = -<<params>>.led_cover_thickness
FEATURE [Part::Part2DObjectPython] Rectangle015  label="gnd_bug_rect"  # Draft 2D object (typed FeaturePython)
  Area = 30
  ChamferSize = 0
  Columns = 1
  FilletRadius = 0
  Height = 3
  Length = 10
  MakeFace = true
  Placement = pos=(-14,-11.5,3) rot=(0,0,1;0rad)
  Rows = 1
  expr: .Placement.Base.x = <<params>>.gnd_bug_x
  expr: .Placement.Base.y = <<params>>.gnd_bug_y
  expr: .Placement.Base.z = <<params>>.housing_back_thickness
  expr: Height = <<params>>.gnd_bug_height
  expr: Length = <<params>>.gnd_bug_width
FEATURE [Part::Extrusion] Extrude017  label="gnd_bug_extr"
  Base = -> Rectangle015
  Dir = (0,0,1)
  DirMode = 2
  FaceMakerClass = Part::FaceMakerBullseye
  FaceMakerMode = 3
  LengthFwd = -1.5
  LengthRev = 0
  Solid = false
  Symmetric = false
  expr: LengthFwd = -<<params>>.gnd_bug_depth
FEATURE [Part::Cut] Cut008  label="housing_bottom"
  Base = -> Cut005
  Refine = true
  Tool = -> Extrude017
FEATURE [Part::Part2DObjectPython] Rectangle019  label="sht_cutout"  # Draft 2D object (typed FeaturePython)
  Area = 3.7854
  ChamferSize = 0
  Columns = 1
  FilletRadius = 0.5
  Height = 2
  Length = 2
  MakeFace = true
  Placement = pos=(-17.52,-3.73,12) rot=(0,0,1;0rad)
  Rows = 1
  expr: .Placement.Base.x = <<params>>.sht_pos_x + <<params>>.sht_width / 2 - <<params>>.sht_cutout_width / 2
  expr: .Placement.Base.y = <<params>>.sht_pos_y + <<params>>.sht_length / 2 - <<params>>.sht_cutout_height / 2
  expr: .Placement.Base.z = <<params>>.housing_back_thickness + <<params>>.housing_middle_height + <<params>>.lid_breakout_offset + <<params>>.lid_top_height
  expr: Height = <<params>>.sht_cutout_height
  expr: Length = <<params>>.sht_cutout_width
FEATURE [Part::Extrusion] Extrude024  label="sht_cutout_extr"
  Base = -> Rectangle019
  Dir = (0,0,1)
  DirMode = 2
  FaceMakerClass = Part::FaceMakerBullseye
  FaceMakerMode = 3
  LengthFwd = -2
  LengthRev = 0
  Solid = false
  Symmetric = false
  expr: LengthFwd = -<<params>>.lid_top_height - <<params>>.lid_inlet_depth
FEATURE [Part::Cut] Cut009  label="lid_w_sht_cutout"
  Base = -> Cut007
  Refine = true
  Tool = -> Extrude024
FEATURE [Part::Part2DObjectPython] Rectangle023  label="sgp_cutout_mid"  # Draft 2D object (typed FeaturePython)
  Area = 8.7854
  ChamferSize = 0
  Columns = 1
  FilletRadius = 0.5
  Height = 4.5
  Length = 2
  MakeFace = true
  Placement = pos=(2.75,-14.05,12) rot=(0,0,1;0rad)
  Rows = 1
  expr: .Placement.Base.x = <<params>>.sgp_pos_x + <<params>>.sgp_width / 2 - <<params>>.sgp_cutout_width / 2
  expr: .Placement.Base.y = <<params>>.led_pos_y + <<params>>.led_height / 2 - <<params>>.sgp_cutout_height / 2
  expr: .Placement.Base.z = <<params>>.housing_back_thickness + <<params>>.housing_middle_height + <<params>>.lid_breakout_offset + <<params>>.lid_top_height
  expr: Height = <<params>>.sgp_cutout_height
  expr: Length = <<params>>.sgp_cutout_width
FEATURE [Part::Extrusion] Extrude025  label="sgp_cutout_mid_extr"
  Base = -> Rectangle023
  Dir = (0,0,1)
  DirMode = 2
  FaceMakerClass = Part::FaceMakerBullseye
  FaceMakerMode = 3
  LengthFwd = -2
  LengthRev = 0
  Solid = false
  Symmetric = false
  expr: LengthFwd = -(<<params>>.lid_top_height + <<params>>.lid_inlet_depth)
FEATURE [Part::Part2DObjectPython] Rectangle024  label="sgp_cutout_left"  # Draft 2D object (typed FeaturePython)
  Area = 8.7854
  ChamferSize = 0
  Columns = 1
  FilletRadius = 0.5
  Height = 4.5
  Length = 2
  MakeFace = true
  Placement = pos=(-2.25,-14.05,12) rot=(0,0,1;0rad)
  Rows = 1
  expr: .Placement.Base.x = <<params>>.sgp_pos_x + <<params>>.sgp_width / 2 - <<params>>.sgp_cutout_width / 2 - <<params>>.cutout_distance
  expr: .Placement.Base.y = <<params>>.led_pos_y + <<params>>.led_height / 2 - <<params>>.sgp_cutout_height / 2
  expr: .Placement.Base.z = <<params>>.housing_back_thickness + <<params>>.housing_middle_height + <<params>>.lid_breakout_offset + <<params>>.lid_top_height
  expr: Height = <<params>>.sgp_cutout_height
  expr: Length = <<params>>.sgp_cutout_width
FEATURE [Part::Extrusion] Extrude026  label="sgp_cutout_left_extr"
  Base = -> Rectangle024
  Dir = (0,0,1)
  DirMode = 2
  FaceMakerClass = Part::FaceMakerBullseye
  FaceMakerMode = 3
  LengthFwd = -2
  LengthRev = 0
  Solid = false
  Symmetric = false
  expr: LengthFwd = -(<<params>>.lid_top_height + <<params>>.lid_inlet_depth)
FEATURE [Part::Part2DObjectPython] Rectangle025  label="sgp_cutout_right"  # Draft 2D object (typed FeaturePython)
  Area = 8.7854
  ChamferSize = 0
  Columns = 1
  FilletRadius = 0.5
  Height = 4.5
  Length = 2
  MakeFace = true
  Placement = pos=(7.75,-14.05,12) rot=(0,0,1;0rad)
  Rows = 1
  expr: .Placement.Base.x = <<params>>.sgp_pos_x + <<params>>.sgp_width / 2 - <<params>>.sgp_cutout_width / 2 + <<params>>.cutout_distance
  expr: .Placement.Base.y = <<params>>.led_pos_y + <<params>>.led_height / 2 - <<params>>.sgp_cutout_height / 2
  expr: .Placement.Base.z = <<params>>.housing_back_thickness + <<params>>.housing_middle_height + <<params>>.lid_breakout_offset + <<params>>.lid_top_height
  expr: Height = <<params>>.sgp_cutout_height
  expr: Length = <<params>>.sgp_cutout_width
FEATURE [Part::Extrusion] Extrude027  label="sgp_cutout_right_extr"
  Base = -> Rectangle025
  Dir = (0,0,1)
  DirMode = 2
  FaceMakerClass = Part::FaceMakerBullseye
  FaceMakerMode = 3
  LengthFwd = -2
  LengthRev = 0
  Solid = false
  Symmetric = false
  expr: LengthFwd = -(<<params>>.lid_top_height + <<params>>.lid_inlet_depth)
FEATURE [Part::Part2DObjectPython] Rectangle026  label="top_cutout_right"  # Draft 2D object (typed FeaturePython)
  Area = 8.7854
  ChamferSize = 0
  Columns = 1
  FilletRadius = 0.5
  Height = 4.5
  Length = 2
  MakeFace = true
  Placement = pos=(7.75,9.55,12) rot=(0,0,1;0rad)
  Rows = 1
  expr: .Placement.Base.x = <<params>>.sgp_pos_x + <<params>>.sgp_width / 2 - <<params>>.sgp_cutout_width / 2 + <<params>>.cutout_distance
  expr: .Placement.Base.y = -(<<params>>.led_pos_y + <<params>>.led_height / 2 - <<params>>.sgp_cutout_height / 2) - <<params>>.sgp_cutout_height
  expr: .Placement.Base.z = <<params>>.housing_back_thickness + <<params>>.housing_middle_height + <<params>>.lid_breakout_offset + <<params>>.lid_top_height
  expr: Height = <<params>>.sgp_cutout_height
  expr: Length = <<params>>.sgp_cutout_width
FEATURE [Part::Extrusion] Extrude028  label="top_cutout_right_extr"
  Base = -> Rectangle026
  Dir = (0,0,1)
  DirMode = 2
  FaceMakerClass = Part::FaceMakerBullseye
  FaceMakerMode = 3
  LengthFwd = -2
  LengthRev = 0
  Solid = false
  Symmetric = false
  expr: LengthFwd = -(<<params>>.lid_top_height + <<params>>.lid_inlet_depth)
FEATURE [Part::Part2DObjectPython] Rectangle027  label="top_cutout_mid"  # Draft 2D object (typed FeaturePython)
  Area = 8.7854
  ChamferSize = 0
  Columns = 1
  FilletRadius = 0.5
  Height = 4.5
  Length = 2
  MakeFace = true
  Placement = pos=(2.75,9.55,12) rot=(0,0,1;0rad)
  Rows = 1
  expr: .Placement.Base.x = <<params>>.sgp_pos_x + <<params>>.sgp_width / 2 - <<params>>.sgp_cutout_width / 2
  expr: .Placement.Base.y = -(<<params>>.led_pos_y + <<params>>.led_height / 2 - <<params>>.sgp_cutout_height / 2) - <<params>>.sgp_cutout_height
  expr: .Placement.Base.z = <<params>>.housing_back_thickness + <<params>>.housing_middle_height + <<params>>.lid_breakout_offset + <<params>>.lid_top_height
  expr: Height = <<params>>.sgp_cutout_height
  expr: Length = <<params>>.sgp_cutout_width
FEATURE [Part::Extrusion] Extrude029  label="top_cutout_mid_extr"
  Base = -> Rectangle027
  Dir = (0,0,1)
  DirMode = 2
  FaceMakerClass = Part::FaceMakerBullseye
  FaceMakerMode = 3
  LengthFwd = -2
  LengthRev = 0
  Solid = false
  Symmetric = false
  expr: LengthFwd = -(<<params>>.lid_top_height + <<params>>.lid_inlet_depth)
FEATURE [Part::Part2DObjectPython] Rectangle028  label="top_cutout_left"  # Draft 2D object (typed FeaturePython)
  Area = 8.7854
  ChamferSize = 0
  Columns = 1
  FilletRadius = 0.5
  Height = 4.5
  Length = 2
  MakeFace = true
  Placement = pos=(-2.25,9.55,12) rot=(0,0,1;0rad)
  Rows = 1
  expr: .Placement.Base.x = <<params>>.sgp_pos_x + <<params>>.sgp_width / 2 - <<params>>.sgp_cutout_width / 2 - <<params>>.cutout_distance
  expr: .Placement.Base.y = -(<<params>>.led_pos_y + <<params>>.led_height / 2 - <<params>>.sgp_cutout_height / 2) - <<params>>.sgp_cutout_height
  expr: .Placement.Base.z = <<params>>.housing_back_thickness + <<params>>.housing_middle_height + <<params>>.lid_breakout_offset + <<params>>.lid_top_height
  expr: Height = <<params>>.sgp_cutout_height
  expr: Length = <<params>>.sgp_cutout_width
FEATURE [Part::Extrusion] Extrude030  label="top_cutout_left_extr"
  Base = -> Rectangle028
  Dir = (0,0,1)
  DirMode = 2
  FaceMakerClass = Part::FaceMakerBullseye
  FaceMakerMode = 3
  LengthFwd = -2
  LengthRev = 0
  Solid = false
  Symmetric = false
  expr: LengthFwd = -(<<params>>.lid_top_height + <<params>>.lid_inlet_depth)
FEATURE [Part::Cut] Cut010
  Base = -> Cut009
  Refine = true
  Tool = -> Extrude025
FEATURE [Part::Cut] Cut011
  Base = -> Cut010
  Refine = true
  Tool = -> Extrude026
FEATURE [Part::Cut] Cut012
  Base = -> Cut011
  Refine = true
  Tool = -> Extrude027
FEATURE [Part::Cut] Cut013
  Base = -> Cut012
  Refine = true
  Tool = -> Extrude028
FEATURE [Part::Cut] Cut014
  Base = -> Cut013
  Refine = true
  Tool = -> Extrude029
FEATURE [Part::Cut] Cut015  label="lid_cutouts"
  Base = -> Cut014
  Refine = true
  Tool = -> Extrude030
FEATURE [Part::Part2DObjectPython] Rectangle029  label="sgp_outer_outline"  # Draft 2D object (typed FeaturePython)
  Area = 58.46
  ChamferSize = 0
  Columns = 1
  FilletRadius = 0
  Height = 7.4
  Length = 7.9
  MakeFace = true
  Placement = pos=(-0.2,-15.18,10) rot=(0,0,1;0rad)
  Rows = 1
  expr: .Placement.Base.x = <<params>>.sgp_pos_x - <<params>>.sep_thickness
  expr: .Placement.Base.y = <<params>>.sgp_pos_y - <<params>>.sep_thickness
  expr: .Placement.Base.z = <<params>>.housing_back_thickness + <<params>>.housing_middle_height + <<params>>.lid_breakout_offset - <<params>>.lid_inlet_depth
  expr: Height = <<params>>.sgp_length + <<params>>.sep_thickness * 2
  expr: Length = <<params>>.sgp_width + <<params>>.sep_thickness * 2
FEATURE [Part::Extrusion] Extrude031  label="sgp_seperator_outer_extr"
  Base = -> Rectangle029
  Dir = (0,0,1)
  DirMode = 2
  FaceMakerClass = Part::FaceMakerBullseye
  FaceMakerMode = 3
  LengthFwd = -4.9
  LengthRev = 0
  Solid = false
  Symmetric = false
  expr: LengthFwd = -<<params>>.housing_middle_height + <<params>>.PCB_height + <<params>>.clearance + <<params>>.lid_inlet_depth
FEATURE [Part::Extrusion] Extrude032  label="sgp_seperator_inner_extr"
  Base = -> Rectangle004
  Dir = (0,0,1)
  DirMode = 2
  FaceMakerClass = Part::FaceMakerBullseye
  FaceMakerMode = 3
  LengthFwd = -4.9
  LengthRev = 0
  Solid = false
  Symmetric = false
  expr: LengthFwd = -<<params>>.housing_middle_height + <<params>>.PCB_height + <<params>>.clearance + <<params>>.lid_inlet_depth
FEATURE [Part::Cut] Cut016  label="sgp_separator_extr"
  Base = -> Extrude031
  Refine = true
  Tool = -> Extrude032
FEATURE [Part::Part2DObjectPython] Rectangle030  label="sht_outer_outline"  # Draft 2D object (typed FeaturePython)
  Area = 58.46
  ChamferSize = 0
  Columns = 1
  FilletRadius = 0
  Height = 7.9
  Length = 7.4
  MakeFace = true
  Placement = pos=(-20.22,-6.68,10) rot=(0,0,1;0rad)
  Rows = 1
  expr: .Placement.Base.x = <<params>>.sht_pos_x - <<params>>.sep_thickness
  expr: .Placement.Base.y = <<params>>.sht_pos_y - <<params>>.sep_thickness
  expr: .Placement.Base.z = <<params>>.housing_back_thickness + <<params>>.housing_middle_height + <<params>>.lid_breakout_offset - <<params>>.lid_inlet_depth
  expr: Height = <<params>>.sht_length + <<params>>.sep_thickness * 2
  expr: Length = <<params>>.sht_width + <<params>>.sep_thickness * 2
FEATURE [Part::Extrusion] Extrude033  label="sht_sep_outer_extr"
  Base = -> Rectangle030
  Dir = (0,0,1)
  DirMode = 2
  FaceMakerClass = Part::FaceMakerBullseye
  FaceMakerMode = 3
  LengthFwd = -4.9
  LengthRev = 0
  Solid = false
  Symmetric = false
  expr: LengthFwd = -<<params>>.housing_middle_height + <<params>>.PCB_height + <<params>>.clearance + <<params>>.lid_inlet_depth
FEATURE [Part::Extrusion] Extrude034  label="sht_sep_inner_extr"
  Base = -> Rectangle005
  Dir = (0,0,1)
  DirMode = 2
  FaceMakerClass = Part::FaceMakerBullseye
  FaceMakerMode = 3
  LengthFwd = -4.9
  LengthRev = 0
  Solid = false
  Symmetric = false
  expr: LengthFwd = -<<params>>.housing_middle_height + <<params>>.PCB_height + <<params>>.clearance + <<params>>.lid_inlet_depth
FEATURE [Part::Cut] Cut017  label="sht_separator_extr"
  Base = -> Extrude033
  Refine = true
  Tool = -> Extrude034
FEATURE [Part::Part2DObjectPython] Circle006  label="led_circle_lid_sep_inner"  # Draft 2D object (typed FeaturePython)
  Area = 38.4845
  FirstAngle = 0
  LastAngle = 0
  MakeFace = true
  Placement = pos=(-9.7,-11.8,10) rot=(0,0,1;0rad)
  Radius = 3.5
  expr: .Placement.Base.x = <<params>>.led_pos_x + <<params>>.led_width / 2
  expr: .Placement.Base.y = <<params>>.led_pos_y + <<params>>.led_height / 2
  expr: .Placement.Base.z = <<params>>.housing_back_thickness + <<params>>.housing_middle_height + <<params>>.lid_breakout_offset - <<params>>.lid_inlet_depth
  expr: Radius = <<params>>.led_circle_dia / 2
FEATURE [Part::Part2DObjectPython] Circle007  label="led_circle_lid_sep_outer"  # Draft 2D object (typed FeaturePython)
  Area = 55.4177
  FirstAngle = 0
  LastAngle = 0
  MakeFace = true
  Placement = pos=(-9.7,-11.8,10) rot=(0,0,1;0rad)
  Radius = 4.2
  expr: .Placement.Base.x = <<params>>.led_pos_x + <<params>>.led_width / 2
  expr: .Placement.Base.y = <<params>>.led_pos_y + <<params>>.led_height / 2
  expr: .Placement.Base.z = <<params>>.housing_back_thickness + <<params>>.housing_middle_height + <<params>>.lid_breakout_offset - <<params>>.lid_inlet_depth
  expr: Radius = <<params>>.led_circle_dia / 2 + <<params>>.sep_thickness
FEATURE [Part::Extrusion] Extrude035  label="led_sep_inner_extr"
  Base = -> Circle006
  Dir = (0,0,1)
  DirMode = 2
  FaceMakerClass = Part::FaceMakerBullseye
  FaceMakerMode = 3
  LengthFwd = -4
  LengthRev = 0
  Solid = false
  Symmetric = false
  expr: LengthFwd = -<<params>>.led_sep_depth
FEATURE [Part::Extrusion] Extrude036  label="led_sep_outer_extr"
  Base = -> Circle007
  Dir = (0,0,1)
  DirMode = 2
  FaceMakerClass = Part::FaceMakerBullseye
  FaceMakerMode = 3
  LengthFwd = -4
  LengthRev = 0
  Solid = false
  Symmetric = false
  expr: LengthFwd = -<<params>>.led_sep_depth
FEATURE [Part::Cut] Cut018  label="led_separator_extr"
  Base = -> Extrude036
  Refine = true
  Tool = -> Extrude035
FEATURE [Part::Part2DObjectPython] Rectangle031  label="press_fit_tr"  # Draft 2D object (typed FeaturePython)
  Area = 1.5
  ChamferSize = 0
  Columns = 1
  FilletRadius = 0
  Height = 1
  Length = 1.5
  MakeFace = true
  Placement = pos=(18.5,9.5,10) rot=(0,0,1;0rad)
  Rows = 1
  expr: .Placement.Base.x = <<params>>.press_fit_pos_x
  expr: .Placement.Base.y = <<params>>.press_fit_pos_y
  expr: .Placement.Base.z = <<params>>.housing_back_thickness + <<params>>.housing_middle_height - <<params>>.lid_inlet_depth + <<params>>.lid_breakout_offset
  expr: Height = <<params>>.press_fit_height
  expr: Length = <<params>>.press_fit_width
FEATURE [Part::Part2DObjectPython] Rectangle032  label="press_fit_bl"  # Draft 2D object (typed FeaturePython)
  Area = 1.5
  ChamferSize = 0
  Columns = 1
  FilletRadius = 0
  Height = 1
  Length = 1.5
  MakeFace = true
  Placement = pos=(-20,-10.5,10) rot=(0,0,1;0.017453rad)
  Rows = 1
  expr: .Placement.Base.x = -<<params>>.press_fit_pos_x - <<params>>.press_fit_width
  expr: .Placement.Base.y = -<<params>>.press_fit_pos_y - <<params>>.press_fit_height
  expr: .Placement.Base.z = <<params>>.housing_back_thickness + <<params>>.housing_middle_height - <<params>>.lid_inlet_depth + <<params>>.lid_breakout_offset
  expr: Height = <<params>>.press_fit_height
  expr: Length = <<params>>.press_fit_width
FEATURE [Part::Extrusion] Extrude037  label="press_fit_tr_extr"
  Base = -> Rectangle031
  Dir = (0,0,1)
  DirMode = 2
  FaceMakerClass = Part::FaceMakerBullseye
  FaceMakerMode = 3
  LengthFwd = -5.15
  LengthRev = 0
  Solid = false
  Symmetric = false
  expr: LengthFwd = -<<params>>.press_fit_length
FEATURE [Part::Extrusion] Extrude038  label="press_fit_bl_extr"
  Base = -> Rectangle032
  Dir = (0,0,1)
  DirMode = 2
  FaceMakerClass = Part::FaceMakerBullseye
  FaceMakerMode = 3
  LengthFwd = -5.15
  LengthRev = 0
  Solid = false
  Symmetric = false
  expr: LengthFwd = -<<params>>.press_fit_length
FEATURE [Part::Fillet] Fillet003  label="press_fit_tr_fillet"
  Base = -> Extrude037
  EdgeLinks = -> Extrude037 [Edge4,Edge10]
  Edges = 2 edges r=0.4: [Edge4,Edge10]
FEATURE [Part::Fillet] Fillet004  label="press_fit_bl_fillet"
  Base = -> Extrude038
  EdgeLinks = -> Extrude038 [Edge4,Edge10]
  Edges = 2 edges r=0.4: [Edge4,Edge10]
FEATURE [Part::Part2DObjectPython] ShapeString  label="VOCS_text"  # Draft 2D object (typed FeaturePython)
  FontFile = <path>
  Fuse = false
  Justification = 6
  JustificationReference = 0
  KeepLeftMargin = false
  MakeFace = true
  ObliqueAngle = 0
  Placement = pos=(-6.45,-7.05,12) rot=(0,0,1;1.5708rad)
  ScaleToSize = true
  Size = 5.8
  String = VOCs
  Tracking = 0
  expr: .Placement.Base.x = <<params>>.led_pos_x + <<params>>.led_width
  expr: .Placement.Base.y = <<params>>.led_pos_y + 8 mm
  expr: .Placement.Base.z = <<params>>.housing_back_thickness + <<params>>.housing_middle_height + <<params>>.lid_top_height + <<params>>.lid_breakout_offset
FEATURE [Part::Extrusion] Extrude039  label="VOCs_text_extr"
  Base = -> ShapeString
  Dir = (0,0,1)
  DirMode = 2
  FaceMakerClass = Part::FaceMakerBullseye
  FaceMakerMode = 3
  LengthFwd = -0.2
  LengthRev = 0
  Solid = false
  Symmetric = false
  expr: LengthFwd = -0.2 mm
FEATURE [Part::Part2DObjectPython] ShapeString001  label="VOCS_text001"  # Draft 2D object (typed FeaturePython)
  FontFile = <path>
  Fuse = false
  Justification = 6
  JustificationReference = 0
  KeepLeftMargin = false
  MakeFace = true
  ObliqueAngle = 0
  Placement = pos=(-6.45,-7.05,12) rot=(0,0,1;1.5708rad)
  ScaleToSize = true
  Size = 5.8
  String = VOCs
  Tracking = 0
  expr: .Placement.Base.x = <<params>>.led_pos_x + <<params>>.led_width
  expr: .Placement.Base.y = <<params>>.led_pos_y + 8 mm
  expr: .Placement.Base.z = <<params>>.housing_back_thickness + <<params>>.housing_middle_height + <<params>>.lid_top_height + <<params>>.lid_breakout_offset
FEATURE [Part::Extrusion] Extrude040  label="VOCs_text_extr_color"
  Base = -> ShapeString001
  Dir = (0,0,1)
  DirMode = 2
  FaceMakerClass = Part::FaceMakerBullseye
  FaceMakerMode = 3
  LengthFwd = -0.2
  LengthRev = 0
  Solid = false
  Symmetric = false
  expr: LengthFwd = -0.2 mm
FEATURE [Part::Cut] Cut019  label="lid_text_cutout"
  Base = -> Cut015
  Refine = true
  Tool = -> Extrude039
FEATURE [Part::Part2DObjectPython] Rectangle033  label="light_sep_substr"  # Draft 2D object (typed FeaturePython)
  Area = 32.5
  ChamferSize = 0
  Columns = 1
  FilletRadius = 0
  Height = -5
  Length = 6.5
  MakeFace = true
  Placement = pos=(-12.95,-15,10) rot=(0,0,1;0rad)
  Rows = 1
  expr: .Placement.Base.x = <<params>>.led_pos_x
  expr: .Placement.Base.y = -<<params>>.PCB_length / 2
  expr: .Placement.Base.z = <<params>>.housing_back_thickness + <<params>>.housing_middle_height + <<params>>.lid_breakout_offset - <<params>>.lid_inlet_depth
  expr: Height = -5 mm
  expr: Length = <<params>>.led_width
FEATURE [Part::Extrusion] Extrude041  label="led_sep_subst_extr"
  Base = -> Rectangle033
  Dir = (0,0,1)
  DirMode = 2
  FaceMakerClass = Part::FaceMakerBullseye
  FaceMakerMode = 3
  LengthFwd = -4
  LengthRev = 0
  Solid = false
  Symmetric = false
  expr: LengthFwd = -<<params>>.led_sep_depth
FEATURE [Part::Cut] Cut020  label="led_sep_cutted"
  Base = -> Cut018
  Refine = true
  Tool = -> Extrude041
note: 2 file-system paths scrubbed to <path> (originals preserved in the JSON sidecar)
